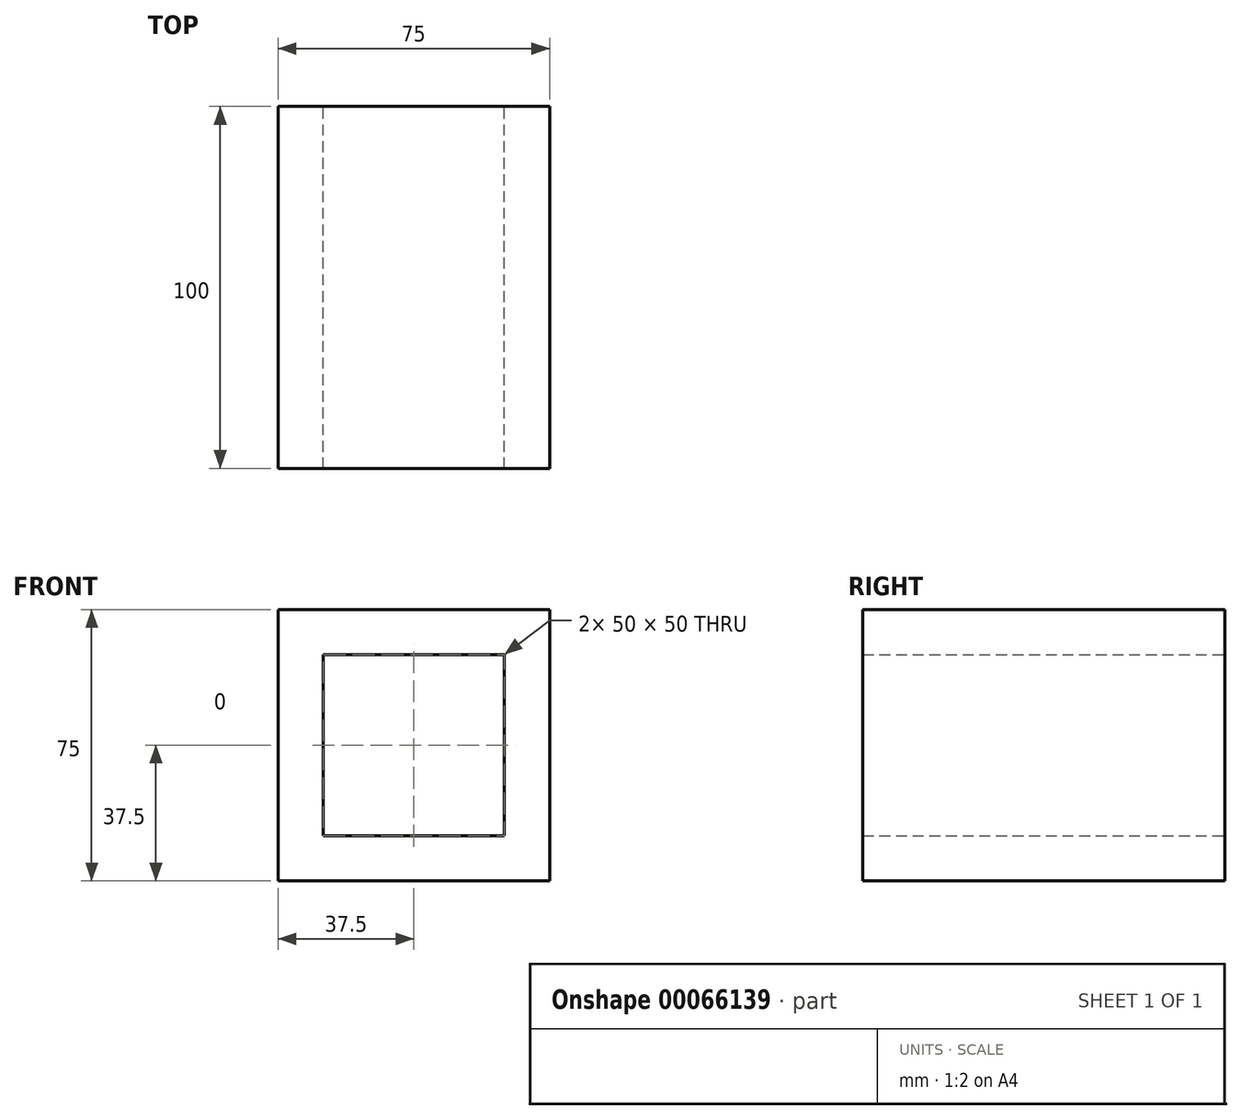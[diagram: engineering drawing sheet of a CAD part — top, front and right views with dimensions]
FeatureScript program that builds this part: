
annotation { "Feature Type Name" : "Feature", "Feature Type Description" : "" }
export const myFeature = defineFeature(function(context is Context, id is Id, definition is map)
    precondition{}
    {
        {
            var Q0;
            Q0=qCreatedBy(makeId("Front.planeOp"),FACE);
            var sketch = newSketch(context, id + "F0", { "sketchPlane" : qUnion([Q0])});
            skLineSegment(sketch, "E0.rect.bottom", {"start": v(-25, 25) * mm, "end": v(25, 25) * mm});
            skLineSegment(sketch, "E0.rect.top", {"start": v(-25, -25) * mm, "end": v(25, -25) * mm});
            skLineSegment(sketch, "E0.rect.left", {"start": v(-25, 25) * mm, "end": v(-25, -25) * mm});
            skLineSegment(sketch, "E0.rect.right", {"start": v(25, 25) * mm, "end": v(25, -25) * mm});
            skPoint(sketch, "E0.rect.middle", {"position": v(0, 0) * mm});
            skLineSegment(sketch, "E1.rect.bottom", {"start": v(37.5, -37.5) * mm, "end": v(-37.5, -37.5) * mm});
            skLineSegment(sketch, "E1.rect.top", {"start": v(37.5, 37.5) * mm, "end": v(-37.5, 37.5) * mm});
            skLineSegment(sketch, "E1.rect.left", {"start": v(37.5, -37.5) * mm, "end": v(37.5, 37.5) * mm});
            skLineSegment(sketch, "E1.rect.right", {"start": v(-37.5, -37.5) * mm, "end": v(-37.5, 37.5) * mm});
            skSolve(sketch);
        }
        {
            var Q0;
            Q0 = qSketchRegion(id + "F0", true);
            extrude(context, id + "F1", {"entities" : qUnion([Q0]), "depth" : 100 * mm});
        }
    });
